# Revit family: 3079382 Feilo Sylvania Lighting Fixture INSTAR PRO LED ADJ WH NW + DB
name_source: partatom
category: Lighting Fixtures
revit_build: Autodesk Revit 2017 (Build: 20190507_1515(x64)
units: mm (PartAtom-declared; Revit-internal decimal feet)

## family parameters
Cut with Voids When Loaded = No
Host = Face
Light Source = No
OmniClass Number = 23.80.70.11.17
OmniClass Title = Specialized Lighting by Location or Use
Part Type = Normal
Room Calculation Point = No
Round Connector Dimension = Use Diameter
Shared = No

## types (1)
- 3079382 INSTAR PRO LED ADJ WH NW + DB
    AccessoryBodyInnerDiameter_FEILO = 72 mm  [stored 0.23622 ft]
    AccessoryBodyOuterDiameter_FEILO = 62 mm  [stored 0.203412 ft]
    AccessoryInnerDiameter_FEILO = 60 mm  [stored 0.19685 ft]
    AccessoryOuterDiameter_FEILO = 90 mm  [stored 0.295276 ft]
    Apparent Load = 13 VA
    Assembly Code = D5020200
    AssetType = Fixed
    CutoutDiameter_FEILO = 75 mm
    Default Elevation = 0 mm  [stored 0 ft]
    Description = Utilsing SunDim technology to acheive warmer colour temperature as the fitting is dimmed. Incredible colour quality with 92  to 94 CRI. 12W LED white downlight. Ideal for hospitality accent and display lighting applications such as bathrooms, wellness areas, terraces or porches. Choice of fixed, adjustable and dimmable fixed versions. Comes complete and ready to install with its driver. Available in white and brushed aluminium finishes. Outstanding performace, up to 545lm - at 3,000K. A small 68mm round cut out is required, giving the ability to place your light source almost anywhere due to a shallow luminaire depth of 49.9mm. Quick and easy to install. No UV or IR radiations. LED technology provides energy efficient solution and reduced maintenance costs
    Diameter_FEILO = 90 mm  [stored 0.295276 ft]
    DocumentationLiterature = http://www.sylvania-lighting.com
    DurationUnit = hours
    ElectricShockClassification = Class II
    ExpectedLife = 50000
    IfcExportAs = IfcLightFixtureType
    IfcExportType = IfcLightFixtureType
    ImpactProtectionIndex = IK02
    IngressProtection = IP20
    InputVoltage = 240V~
    Keynote = 16500
    Lamp = LED
    LampColourRenderingIndex = 0
    LampColourTemperature = 4000 K
    LampNominalLuminous = 810 lm
    LampsType = LED
    LightOutputRatio = 100
    LuminousEfficacy = 60 lm/W
    Manufacturer = Feilo Sylvania
    ManufacturerName = Feilo Sylvania
    Material = aluminium housing, glass diffuser
    Material_1_FEILO = Aluminum_Sylvania_Instar Eco Kit Adjustable SunDim_Bright
    Material_2_FEILO = Aluminum_Sylvania_Instar Eco Kit Adjustable SunDim_White
    Material_3_FEILO = Aluminum_Sylvania_Instar Eco Kit Adjustable SunDim_White
    Material_4_FEILO = Glass_Sylvania_Instar Eco Kit Adjustable SunDim_Clear
    Model = INSTAR PRO LED ADJ WH NW + DB
    ModelNumber = 3079382
    ModelReference = INSTAR PRO LED ADJ WH NW + DB
    Name = INSTAR PRO LED ADJ WH NW + DB
    NominalHeight = 60 mm  [stored 0.19685 ft]
    NominalLength = 90 mm  [stored 0.295276 ft]
    NominalWidth = 0 mm  [stored 0 ft]
    Offset_FEILO = -5.3 mm
    PowerConsumption = 13 W
    PowerFactor = 0
    RecessedDepth_FEILO = 138 mm
    TypeHead_FEILO = Instar Pro Rotateable Head : 3079382 INSTAR PRO LED ADJ WH NW + DB
    TypeName = INSTAR PRO LED ADJ WH NW + DB
    URL = http://www.sylvania-lighting.com
    Voltage = 240 V
    Weight = 6.62 kg

note: [stored X ft] marks values corroborated as IEEE doubles in the binary element streams (Revit-internal decimal feet)

## geometry (parser evidence)
native form markers: Sweep x4
no freeform markers — native parametric forms only
